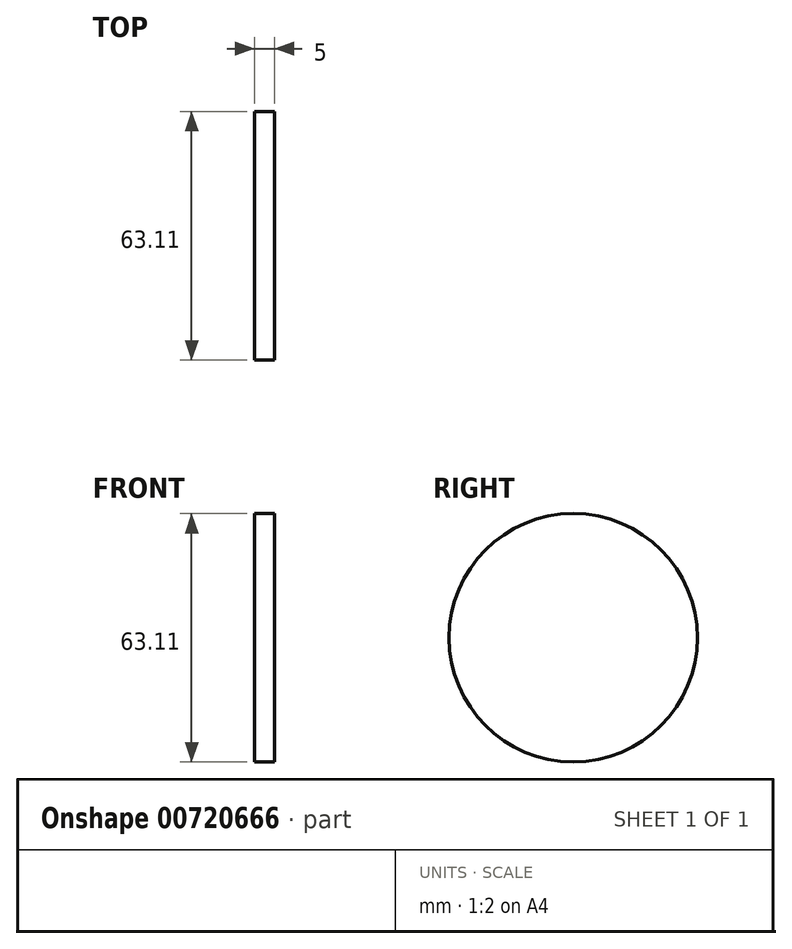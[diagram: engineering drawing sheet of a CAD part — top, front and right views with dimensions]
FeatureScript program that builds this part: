
annotation { "Feature Type Name" : "Feature", "Feature Type Description" : "" }
export const myFeature = defineFeature(function(context is Context, id is Id, definition is map)
    precondition{}
    {
        {
            var Q0;
            Q0=qCreatedBy(makeId("Right.planeOp"),FACE);
            var sketch = newSketch(context, id + "F0", { "sketchPlane" : qUnion([Q0])});
            skCircle(sketch, "E0", {"center": v(-56.3, 44.26) * mm, "radius": 31.56 * mm});
            skSolve(sketch);
        }
        {
            var Q0;
            Q0 = qSketchRegion(id + "F0", true);
            extrude(context, id + "F1", {"entities" : qUnion([Q0]), "depth" : 5 * mm, "offsetDistance" : 25.4 * mm});
        }
    });
